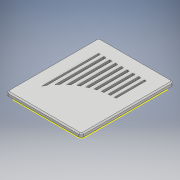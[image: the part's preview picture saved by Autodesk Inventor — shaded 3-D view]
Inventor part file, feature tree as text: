
AUTODESK INVENTOR PART (.ipt)
format: ipt  version: 2017 (Build 210142000, 142)  size: 222,208 bytes
history: native  units: mm
features: sketch x4, reference x4, other x3, extrude x2, plane x1, chamfer x1
ambient origin geometry x8: Origin, YZ Plane, XZ Plane, XY Plane, X Axis, Y Axis, Z Axis, Center Point
bodies: Solid1 (feature_tree)
feature tree (15):
  extrude  "Extrusion1"  Depth=3.0mm TaperAngle=0.0deg
  extrude  "Extrusion2"  Depth=20.0mm TaperAngle=60.0deg
  plane  "Work Plane1"
  sketch  "3D Sketch1"
  chamfer  "Chamfer1"  Distance=60.0mm
  other  "Grill1"
  sketch  "Sketch1"  dims[d0=3.0mm d1=0.0mm d2=2.5mm d3=0.0mm]
  reference  "Reference1"
  reference  "Reference2"
  reference  "Reference3"
  sketch  "Sketch2"  dims[d4=20.0mm d10=1.0mm d11=2.0mm d12=60.0deg]
  reference  "Reference4"
  sketch  "Sketch5"  dims[d13=45.0mm d14=60.0mm d15=11.25mm d16=5.0mm d17=5.0mm d18=5.0mm d19=5.0mm d20=5.0mm d21=5.0mm d22=5.0mm d23=5.0mm d24=2.002063mm d25=3.0mm d26=3.0mm d27=0.0mm d28=1.0mm d29=3.0mm d30=0.0mm d31=3.0mm d32=0.0mm d33=0.0mm d34=1.0mm d35=0.0mm d36=0.0mm d37=0.0mm d38=55.484114mm]
  other  "Assembly1"
  other  "SmallCase:1"
